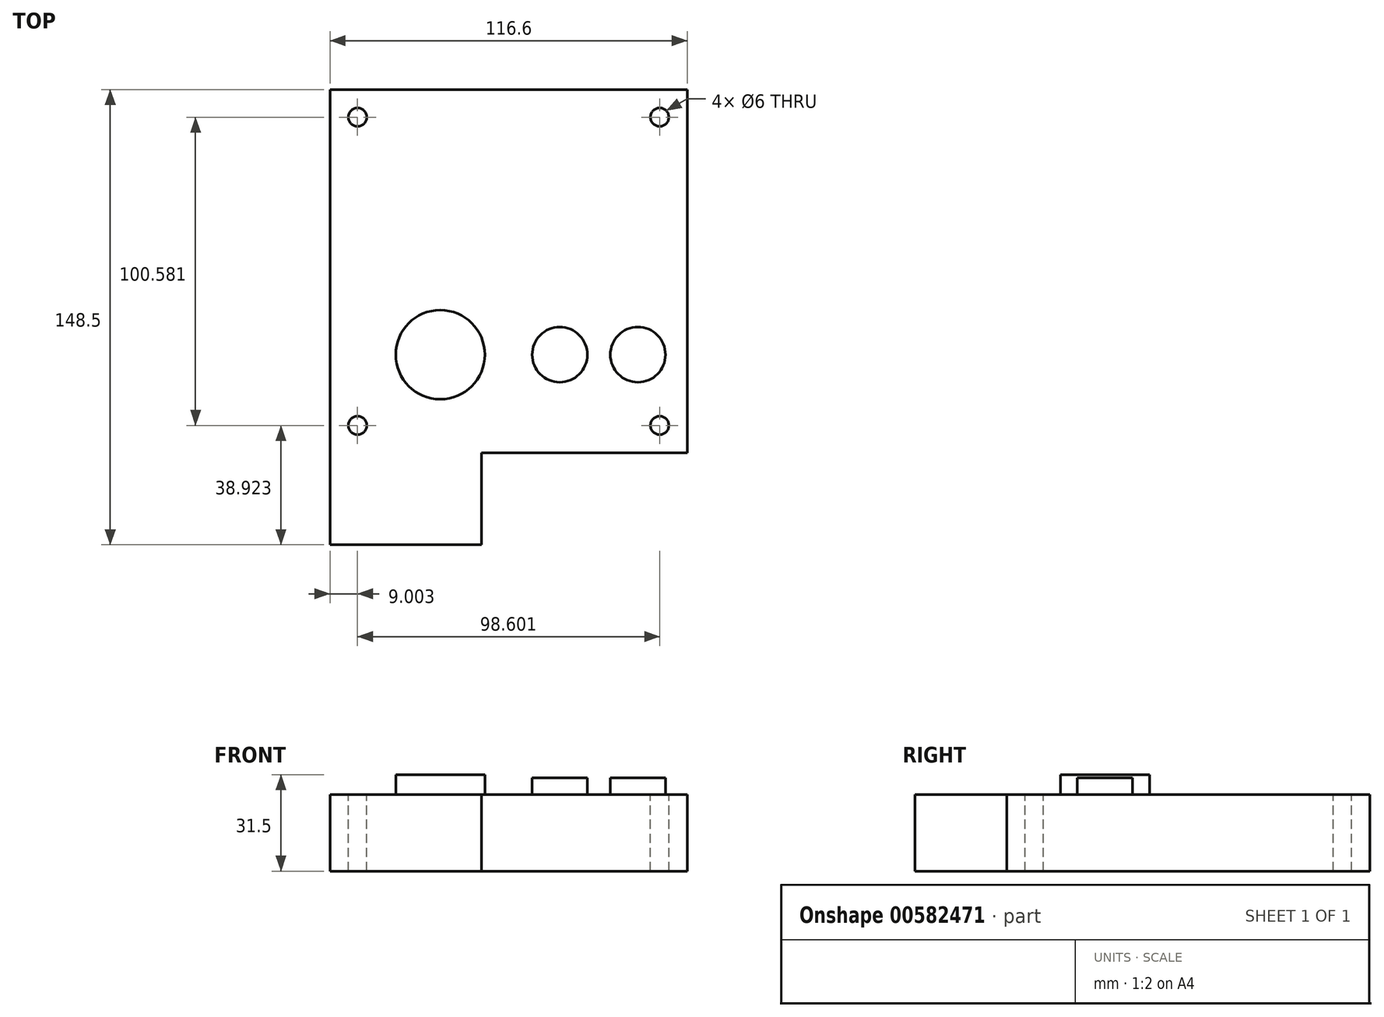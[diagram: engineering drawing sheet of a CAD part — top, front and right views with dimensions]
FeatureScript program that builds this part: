
annotation { "Feature Type Name" : "Feature", "Feature Type Description" : "" }
export const myFeature = defineFeature(function(context is Context, id is Id, definition is map)
    precondition{}
    {
        {
            var Q0;
            Q0=qCreatedBy(makeId("Top.planeOp"),FACE);
            var sketch = newSketch(context, id + "F0", { "sketchPlane" : qUnion([Q0])});
            skLineSegment(sketch, "E0.top", {"start": v(16.06, 100.3) * mm, "end": v(-100.54, 100.3) * mm});
            skLineSegment(sketch, "E0.left", {"start": v(16.06, -18.2) * mm, "end": v(16.06, 100.3) * mm});
            skLineSegment(sketch, "E1", {"start": v(-100.54, 100.3) * mm, "end": v(-100.54, -48.2) * mm});
            skLineSegment(sketch, "E2", {"start": v(-100.54, -48.2) * mm, "end": v(-51.04, -48.2) * mm});
            skLineSegment(sketch, "E3", {"start": v(-51.04, -48.2) * mm, "end": v(-51.04, -18.2) * mm});
            skLineSegment(sketch, "E4", {"start": v(-51.04, -18.2) * mm, "end": v(16.06, -18.2) * mm});
            skSolve(sketch);
        }
        {
            var Q0;
            Q0=makeQuery(id+"F0.imprint","IMPRINT",FACE,{"disambiguationData":[TD([[makeQuery(id+"F0.imprint","IMPRINT",EDGE,{"derivedFrom":sQuery(id+"F0.wireOp",EDGE,"E0.top")}),1.0]])]});
            extrude(context, id + "F1", {"entities" : qUnion([Q0]), "depth" : 25 * mm, "offsetDistance" : 25 * mm});
        }
        {
            var Q0;
            Q0=makeQuery(id+"F1.opExtrude","CAP_FACE",FACE,{"disambiguationData":[OSD([sQuery(id+"F0.wireOp",EDGE,"E0.top"),sQuery(id+"F0.wireOp",EDGE,"E0.left"),sQuery(id+"F0.wireOp",EDGE,"E1"),sQuery(id+"F0.wireOp",EDGE,"E2"),sQuery(id+"F0.wireOp",EDGE,"E3"),sQuery(id+"F0.wireOp",EDGE,"E4")])],"isStart":false});
            var sketch = newSketch(context, id + "F2", { "sketchPlane" : qUnion([Q0])});
            skLineSegment(sketch, "E5", {"start": v(-100.54, 100.3) * mm, "end": v(-100.54, 91.3) * mm});
            skCircle(sketch, "E6", {"center": v(-91.54, 91.3) * mm, "radius": 3 * mm});
            skLineSegment(sketch, "E7", {"start": v(16.06, 100.3) * mm, "end": v(7.06, 100.3) * mm});
            skCircle(sketch, "E8", {"center": v(7.06, 91.3) * mm, "radius": 3 * mm});
            skCircle(sketch, "E9", {"center": v(7.06, -9.29) * mm, "radius": 3 * mm});
            skCircle(sketch, "E10", {"center": v(-91.54, -9.29) * mm, "radius": 3 * mm});
            skPoint(sketch, "E11.orphan", {"position": v(7.06, -18.2) * mm});
            skPoint(sketch, "E12.trimOffspring.end.orphan", {"position": v(-94.78, -9.29) * mm});
            skSolve(sketch);
        }
        {
            var Q0;
            Q0=makeQuery(id+"F2.imprint","IMPRINT",FACE,{"disambiguationData":[TD([[makeQuery(id+"F2.imprint","IMPRINT",EDGE,{"derivedFrom":sQuery(id+"F2.wireOp",EDGE,"E8")}),1.0]])]});
            var Q1;
            Q1=makeQuery(id+"F2.imprint","IMPRINT",FACE,{"disambiguationData":[TD([[makeQuery(id+"F2.imprint","IMPRINT",EDGE,{"derivedFrom":sQuery(id+"F2.wireOp",EDGE,"E9")}),1.0]])]});
            var Q2;
            Q2=makeQuery(id+"F2.imprint","IMPRINT",FACE,{"disambiguationData":[TD([[makeQuery(id+"F2.imprint","IMPRINT",EDGE,{"derivedFrom":sQuery(id+"F2.wireOp",EDGE,"E6")}),1.0]])]});
            var Q3;
            Q3=makeQuery(id+"F2.imprint","IMPRINT",FACE,{"disambiguationData":[TD([[makeQuery(id+"F2.imprint","IMPRINT",EDGE,{"derivedFrom":sQuery(id+"F2.wireOp",EDGE,"E10")}),1.0]])]});
            extrude(context, id + "F3", {"entities" : qUnion([Q0, Q1, Q2, Q3]), "operationType" : NewBodyOperationType.REMOVE, "oppositeDirection" : true, "depth" : 1000 * mm, "offsetDistance" : 25 * mm});
        }
        {
            var Q0;
            Q0=makeQuery(id+"F1.opExtrude","CAP_FACE",FACE,{"disambiguationData":[OSD([sQuery(id+"F0.wireOp",EDGE,"E0.top"),sQuery(id+"F0.wireOp",EDGE,"E0.left"),sQuery(id+"F0.wireOp",EDGE,"E1"),sQuery(id+"F0.wireOp",EDGE,"E2"),sQuery(id+"F0.wireOp",EDGE,"E3"),sQuery(id+"F0.wireOp",EDGE,"E4")])],"isStart":false});
            var sketch = newSketch(context, id + "F4", { "sketchPlane" : qUnion([Q0])});
            skCircle(sketch, "E13", {"center": v(-64.54, 13.8) * mm, "radius": 14.54 * mm});
            skPoint(sketch, "E14.end.orphan", {"position": v(16.06, 13.8) * mm});
            skSolve(sketch);
        }
        {
            var Q0;
            Q0=makeQuery(id+"F4.imprint","IMPRINT",FACE,{"disambiguationData":[TD([[makeQuery(id+"F4.imprint","IMPRINT",EDGE,{"derivedFrom":sQuery(id+"F4.wireOp",EDGE,"E13")}),1.0]])]});
            extrude(context, id + "F5", {"entities" : qUnion([Q0]), "operationType" : NewBodyOperationType.ADD, "depth" : 6.5 * mm, "offsetDistance" : 25 * mm});
        }
        {
            var Q0;
            Q0=makeQuery(id+"F1.opExtrude","CAP_FACE",FACE,{"disambiguationData":[OSD([sQuery(id+"F0.wireOp",EDGE,"E0.top"),sQuery(id+"F0.wireOp",EDGE,"E0.left"),sQuery(id+"F0.wireOp",EDGE,"E1"),sQuery(id+"F0.wireOp",EDGE,"E2"),sQuery(id+"F0.wireOp",EDGE,"E3"),sQuery(id+"F0.wireOp",EDGE,"E4")])],"isStart":false});
            var sketch = newSketch(context, id + "F6", { "sketchPlane" : qUnion([Q0])});
            skCircle(sketch, "E15", {"center": v(-25.54, 13.8) * mm, "radius": 9 * mm});
            skCircle(sketch, "E16", {"center": v(-0.04, 13.8) * mm, "radius": 9 * mm});
            skPoint(sketch, "E17.orphan", {"position": v(-64.54, 13.8) * mm});
            skSolve(sketch);
        }
        {
            var Q0;
            Q0=makeQuery(id+"F6.imprint","IMPRINT",FACE,{"disambiguationData":[TD([[makeQuery(id+"F6.imprint","IMPRINT",EDGE,{"derivedFrom":sQuery(id+"F6.wireOp",EDGE,"E16")}),1.0]])]});
            var Q1;
            Q1=makeQuery(id+"F6.imprint","IMPRINT",FACE,{"disambiguationData":[TD([[makeQuery(id+"F6.imprint","IMPRINT",EDGE,{"derivedFrom":sQuery(id+"F6.wireOp",EDGE,"E15")}),1.0]])]});
            extrude(context, id + "F7", {"entities" : qUnion([Q0, Q1]), "operationType" : NewBodyOperationType.ADD, "depth" : 5.4 * mm, "offsetDistance" : 25 * mm});
        }
    });
